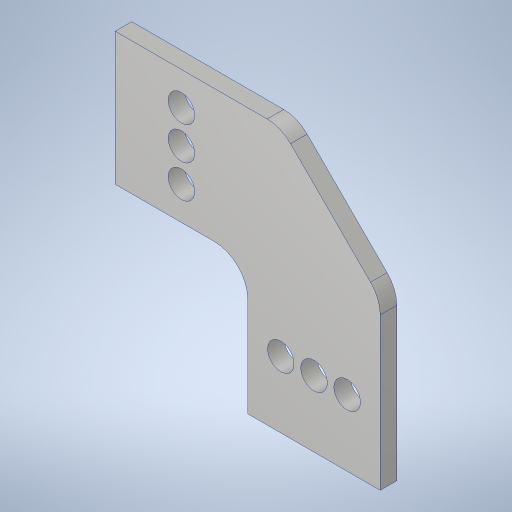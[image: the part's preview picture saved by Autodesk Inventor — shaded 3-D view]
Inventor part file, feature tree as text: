
AUTODESK INVENTOR PART (.ipt)
format: ipt  version: 2023.4 (Build 274418000, 418)  size: 266,240 bytes
history: native  units: in
note: dims shown in document units (in); Inventor stores cm internally (conversion verified against a paired STEP export)
features: sketch x1, extrude x1, hole x1, chamfer x1, fillet x1
ambient origin geometry x8: Origin, YZ Plane, XZ Plane, XY Plane, X Axis, Y Axis, Z Axis, Center Point
bodies: Solid1 (feature_tree)
feature tree (5):
  sketch  "Sketch1"  dims[d0=1.0in d1=3.0in d2=3.0in d3=1.0in d4=1.25in d5=0.25in d6=0.25in d7=0.25in d8=0.25in d9=1.25in d10=1.0in d11=1.0in d12=0.125in d13=0.0in d14=0.201in d15=0.75in d16=0.385in d17=0.25in d18=0.5635in d19=1.0in d20=0.8108in d22=0.75in d23=0.125in d24=45.0deg d25=0.25in]
  extrude  "Extrusion1"  Depth=0.25in
  hole  "Hole1"  [1 undecoded]
  chamfer  "Chamfer1"  Distance=1.0in
  fillet  "Fillet2"  Radius=1.25in
note: 1 required parameter value undecoded (feature->parameter linkage not recoverable at this tier; creation-order binding heuristic only, values carry confidence <= 0.55)
